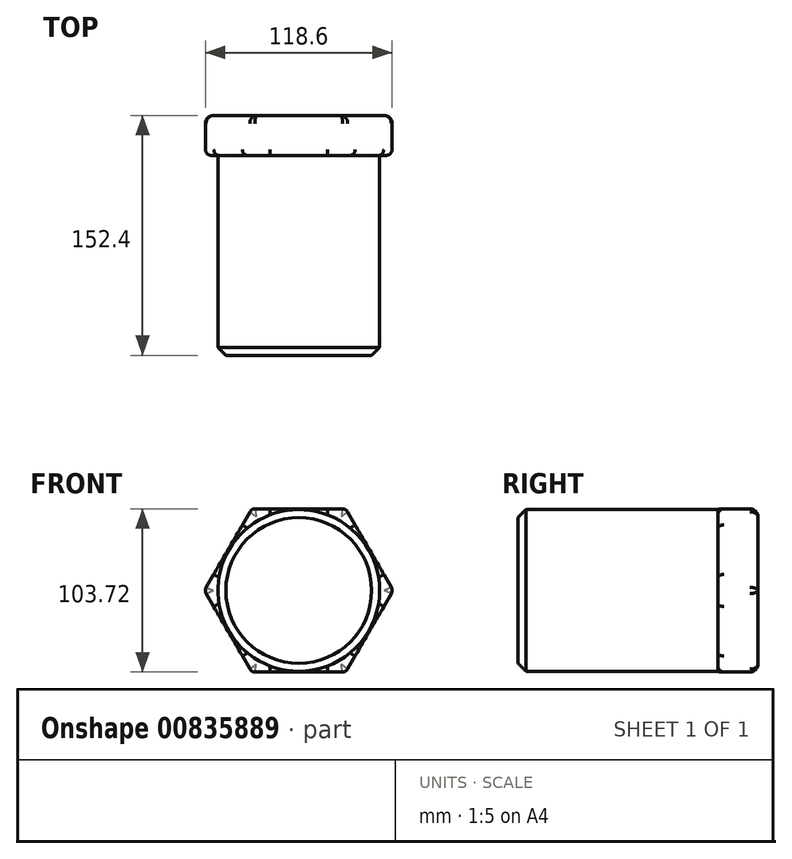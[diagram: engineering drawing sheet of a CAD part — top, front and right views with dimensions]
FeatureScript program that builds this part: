
annotation { "Feature Type Name" : "Feature", "Feature Type Description" : "" }
export const myFeature = defineFeature(function(context is Context, id is Id, definition is map)
    precondition{}
    {
        {
            var Q0;
            Q0=qCreatedBy(makeId("Front.planeOp"),FACE);
            var sketch = newSketch(context, id + "F0", { "sketchPlane" : qUnion([Q0])});
            skCircle(sketch, "E0", {"center": v(0, 0) * mm, "radius": 51.36 * mm});
            skCircle(sketch, "E1.cCircle", {"center": v(0, 0) * mm, "radius": 51.36 * mm, "construction": true});
            skLineSegment(sketch, "E1.0", {"start": v(51.36, 29.65) * mm, "end": v(51.36, -29.65) * mm});
            skLineSegment(sketch, "E1.1", {"start": v(51.36, -29.65) * mm, "end": v(0, -59.3) * mm});
            skLineSegment(sketch, "E1.2", {"start": v(0, -59.3) * mm, "end": v(-51.36, -29.65) * mm});
            skLineSegment(sketch, "E1.3", {"start": v(-51.36, -29.65) * mm, "end": v(-51.36, 29.65) * mm});
            skLineSegment(sketch, "E1.4", {"start": v(-51.36, 29.65) * mm, "end": v(0, 59.3) * mm});
            skLineSegment(sketch, "E1.5", {"start": v(0, 59.3) * mm, "end": v(51.36, 29.65) * mm});
            skPoint(sketch, "E1.0.midPoint", {"position": v(51.36, 0) * mm});
            skSolve(sketch);
        }
        {
            var Q0;
            {var subQ0=sQuery(id+"F0.wireOp",EDGE,"E0");var subQ4=makeQuery(id+"F0.imprint","INTERSECT",VERTEX,{"derivedFrom":[subQ0,sQuery(id+"F0.wireOp",EDGE,"E1.5")]});Q0=makeQuery(id+"F0.imprint","IMPRINT",FACE,{"disambiguationData":[TD([[makeQuery(id+"F0.imprint","IMPRINT",EDGE,{"disambiguationData":[TD([[subQ4,1.0]])],"derivedFrom":subQ0}),1.0]])]});}
            extrude(context, id + "F1", {"entities" : qUnion([Q0]), "depth" : 127 * mm, "offsetDistance" : 25.4 * mm});
        }
        {
            var Q0;
            Q0=qCreatedBy(makeId("Front.planeOp"),FACE);
            var sketch = newSketch(context, id + "F2", { "sketchPlane" : qUnion([Q0])});
            skCircle(sketch, "E2.cCircle", {"center": v(0, 0) * mm, "radius": 51.86 * mm, "construction": true});
            skLineSegment(sketch, "E2.0", {"start": v(-29.94, 51.86) * mm, "end": v(29.94, 51.86) * mm});
            skLineSegment(sketch, "E2.1", {"start": v(29.94, 51.86) * mm, "end": v(59.88, 0) * mm});
            skLineSegment(sketch, "E2.2", {"start": v(59.88, 0) * mm, "end": v(29.94, -51.86) * mm});
            skLineSegment(sketch, "E2.3", {"start": v(29.94, -51.86) * mm, "end": v(-29.94, -51.86) * mm});
            skLineSegment(sketch, "E2.4", {"start": v(-29.94, -51.86) * mm, "end": v(-59.88, 0) * mm});
            skLineSegment(sketch, "E2.5", {"start": v(-59.88, 0) * mm, "end": v(-29.94, 51.86) * mm});
            skPoint(sketch, "E2.0.midPoint", {"position": v(0, 51.86) * mm});
            skSolve(sketch);
        }
        {
            var Q0;
            Q0=makeQuery(id+"F2.imprint","IMPRINT",FACE,{"disambiguationData":[TD([[makeQuery(id+"F2.imprint","IMPRINT",EDGE,{"derivedFrom":sQuery(id+"F2.wireOp",EDGE,"E2.0")}),-1.0]])]});
            extrude(context, id + "F3", {"entities" : qUnion([Q0]), "operationType" : NewBodyOperationType.ADD, "oppositeDirection" : true, "depth" : 25.4 * mm, "offsetDistance" : 25.4 * mm});
        }
        {
            var Q0;
            Q0=makeQuery(id+"F3.opExtrude","CAP_FACE",FACE,{"disambiguationData":[OSD([sQuery(id+"F2.wireOp",EDGE,"E2.0"),sQuery(id+"F2.wireOp",EDGE,"E2.1"),sQuery(id+"F2.wireOp",EDGE,"E2.2"),sQuery(id+"F2.wireOp",EDGE,"E2.3"),sQuery(id+"F2.wireOp",EDGE,"E2.4"),sQuery(id+"F2.wireOp",EDGE,"E2.5")])],"isStart":false});
            fillet(context, id + "F4", {"entities" : qUnion([Q0]), "radius" : 5.08 * mm, "tangentPropagation" : true, "allowEdgeOverflow" : false});
        }
        {
            var Q0;
            Q0=makeQuery(id+"F3.opExtrude","SWEPT_EDGE",EDGE,{"disambiguationData":[OSD([sQuery(id+"F2.wireOp",EDGE,"E2.0"),sQuery(id+"F2.wireOp",EDGE,"E2.1")])]});
            var Q1;
            Q1=makeQuery(id+"F3.opExtrude","SWEPT_EDGE",EDGE,{"disambiguationData":[OSD([sQuery(id+"F2.wireOp",EDGE,"E2.1"),sQuery(id+"F2.wireOp",EDGE,"E2.2")])]});
            var Q2;
            Q2=makeQuery(id+"F3.opExtrude","SWEPT_EDGE",EDGE,{"disambiguationData":[OSD([sQuery(id+"F2.wireOp",EDGE,"E2.0"),sQuery(id+"F2.wireOp",EDGE,"E2.5")])]});
            var Q3;
            Q3=makeQuery(id+"F3.opExtrude","SWEPT_FACE",FACE,{"disambiguationData":[OSD([sQuery(id+"F2.wireOp",EDGE,"E2.3")])]});
            var Q4;
            Q4=makeQuery(id+"F3.opExtrude","SWEPT_FACE",FACE,{"disambiguationData":[OSD([sQuery(id+"F2.wireOp",EDGE,"E2.2")])]});
            var Q5;
            Q5=makeQuery(id+"F3.opExtrude","SWEPT_FACE",FACE,{"disambiguationData":[OSD([sQuery(id+"F2.wireOp",EDGE,"E2.4")])]});
            var Q6;
            Q6=makeQuery(id+"F3.opExtrude","SWEPT_FACE",FACE,{"disambiguationData":[OSD([sQuery(id+"F2.wireOp",EDGE,"E2.1")])]});
            var Q7;
            Q7=makeQuery(id+"F3.opExtrude","SWEPT_FACE",FACE,{"disambiguationData":[OSD([sQuery(id+"F2.wireOp",EDGE,"E2.0")])]});
            var Q8;
            Q8=makeQuery(id+"F3.opExtrude","SWEPT_FACE",FACE,{"disambiguationData":[OSD([sQuery(id+"F2.wireOp",EDGE,"E2.5")])]});
            fillet(context, id + "F5", {"entities" : qUnion([Q0, Q1, Q2, Q3, Q4, Q5, Q6, Q7, Q8]), "radius" : 3.8 * mm, "tangentPropagation" : true, "allowEdgeOverflow" : false});
        }
        {
            var Q0;
            Q0=makeQuery(id+"F1.opExtrude","CAP_EDGE",EDGE,{"disambiguationData":[OSD([sQuery(id+"F0.wireOp",EDGE,"E0")])],"isStart":false});
            chamfer(context, id + "F6", {"entities" : qUnion([Q0]), "width" : 5.08 * mm, "tangentPropagation" : true});
        }
    });
